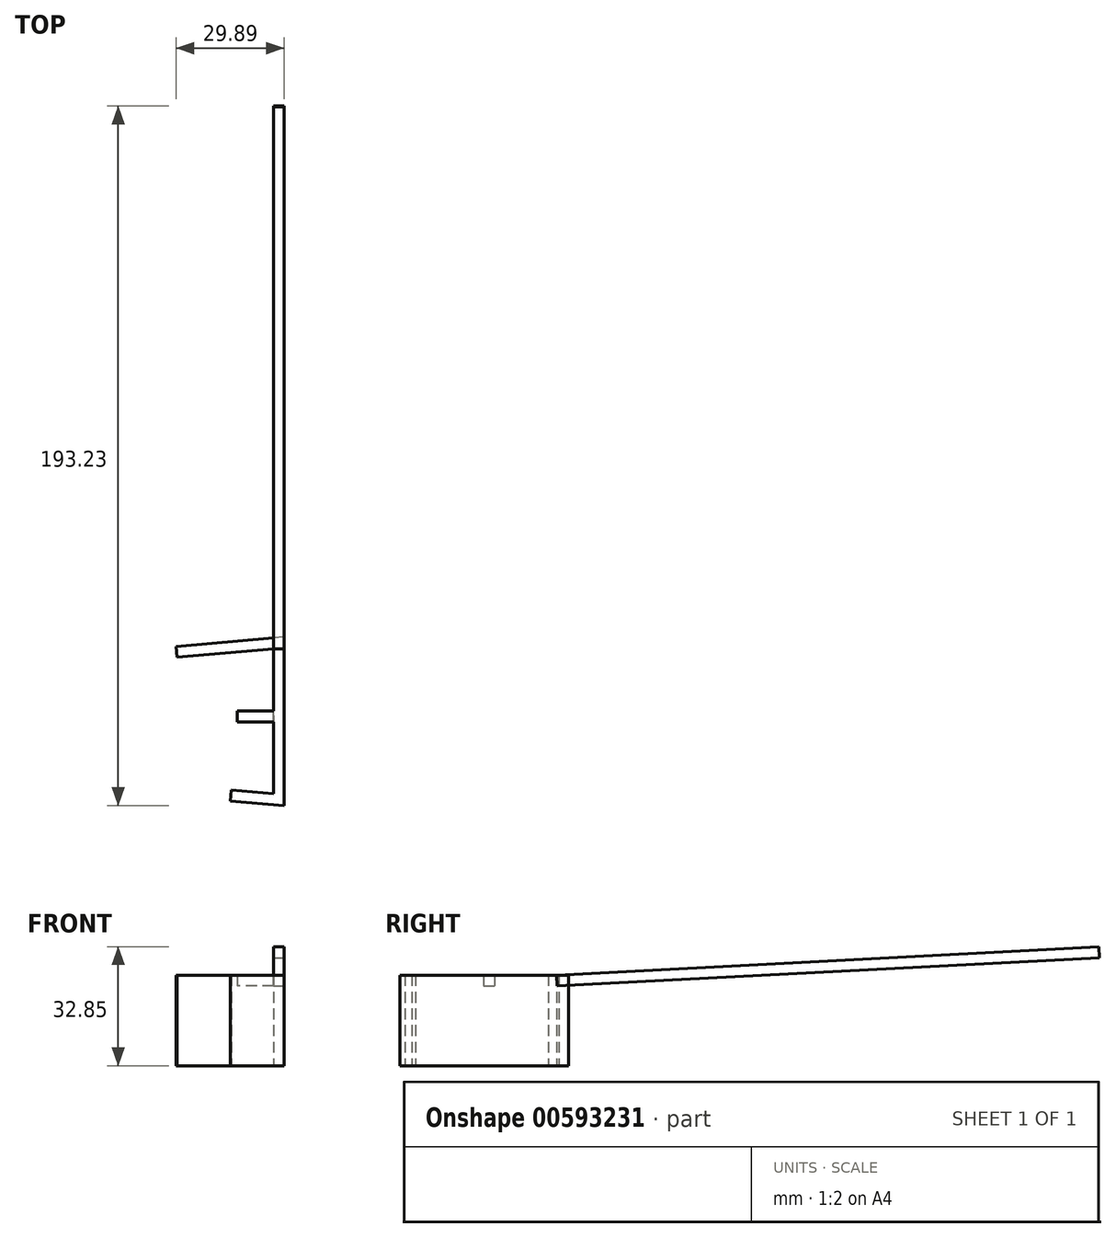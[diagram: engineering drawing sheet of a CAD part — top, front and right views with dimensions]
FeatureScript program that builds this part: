
annotation { "Feature Type Name" : "Feature", "Feature Type Description" : "" }
export const myFeature = defineFeature(function(context is Context, id is Id, definition is map)
    precondition{}
    {
        {
            var Q0;
            Q0=qCreatedBy(makeId("Top.planeOp"),FACE);
            var sketch = newSketch(context, id + "F0", { "sketchPlane" : qUnion([Q0])});
            skLineSegment(sketch, "E0", {"start": v(0, 0) * mm, "end": v(0, 46.55) * mm});
            skLineSegment(sketch, "E1", {"start": v(0, 46.55) * mm, "end": v(-29.89, 43.93) * mm});
            skLineSegment(sketch, "E2", {"start": v(-29.89, 43.93) * mm, "end": v(-29.62, 40.94) * mm});
            skLineSegment(sketch, "E3", {"start": v(-29.62, 40.94) * mm, "end": v(-3, 43.27) * mm});
            skLineSegment(sketch, "E4", {"start": v(-3, 43.27) * mm, "end": v(-3, 3.27) * mm});
            skLineSegment(sketch, "E5", {"start": v(-3, 3.27) * mm, "end": v(-14.68, 4.3) * mm});
            skLineSegment(sketch, "E6", {"start": v(-14.68, 4.3) * mm, "end": v(-14.94, 1.3) * mm});
            skLineSegment(sketch, "E7", {"start": v(-14.94, 1.3) * mm, "end": v(0, 0) * mm});
            skLineSegment(sketch, "E8", {"start": v(0, 0) * mm, "end": v(0, 0) * mm});
            skSolve(sketch);
        }
        {
            var Q0;
            Q0 = qSketchRegion(id + "F0", true);
            extrude(context, id + "F1", {"entities" : qUnion([Q0]), "depth" : 25 * mm, "offsetDistance" : 25 * mm});
        }
        {
            var Q0;
            Q0=qCreatedBy(makeId("Top.planeOp"),FACE);
            var sketch = newSketch(context, id + "F2", { "sketchPlane" : qUnion([Q0])});
            skLineSegment(sketch, "E9", {"start": v(-3, 26.12) * mm, "end": v(-13, 26.12) * mm});
            skLineSegment(sketch, "E10", {"start": v(-13, 26.12) * mm, "end": v(-13, 23.12) * mm});
            skLineSegment(sketch, "E11", {"start": v(-13, 23.12) * mm, "end": v(-3, 23.12) * mm});
            skLineSegment(sketch, "E12", {"start": v(-3, 23.12) * mm, "end": v(-3, 26.12) * mm});
            skSolve(sketch);
        }
        {
            var Q0;
            Q0 = qSketchRegion(id + "F2", true);
            extrude(context, id + "F3", {"entities" : qUnion([Q0]), "operationType" : NewBodyOperationType.ADD, "depth" : 25 * mm, "offsetDistance" : 25 * mm, "hasSecondDirection" : true, "secondDirectionOppositeDirection" : false, "secondDirectionDepth" : 22 * mm});
        }
        {
            var Q0;
            Q0=qCreatedBy(makeId("Right.planeOp"),FACE);
            var sketch = newSketch(context, id + "F4", { "sketchPlane" : qUnion([Q0])});
            skLineSegment(sketch, "E13.bottom", {"start": v(43.27, 25) * mm, "end": v(193.07, 32.85) * mm});
            skLineSegment(sketch, "E13.top", {"start": v(43.43, 22) * mm, "end": v(193.23, 29.85) * mm});
            skLineSegment(sketch, "E13.left", {"start": v(43.27, 25) * mm, "end": v(43.43, 22) * mm});
            skLineSegment(sketch, "E13.right", {"start": v(193.07, 32.85) * mm, "end": v(193.23, 29.85) * mm});
            skSolve(sketch);
        }
        {
            var Q0;
            Q0 = qSketchRegion(id + "F4", true);
            extrude(context, id + "F5", {"entities" : qUnion([Q0]), "oppositeDirection" : true, "depth" : 3 * mm, "offsetDistance" : 25 * mm});
        }
    });
